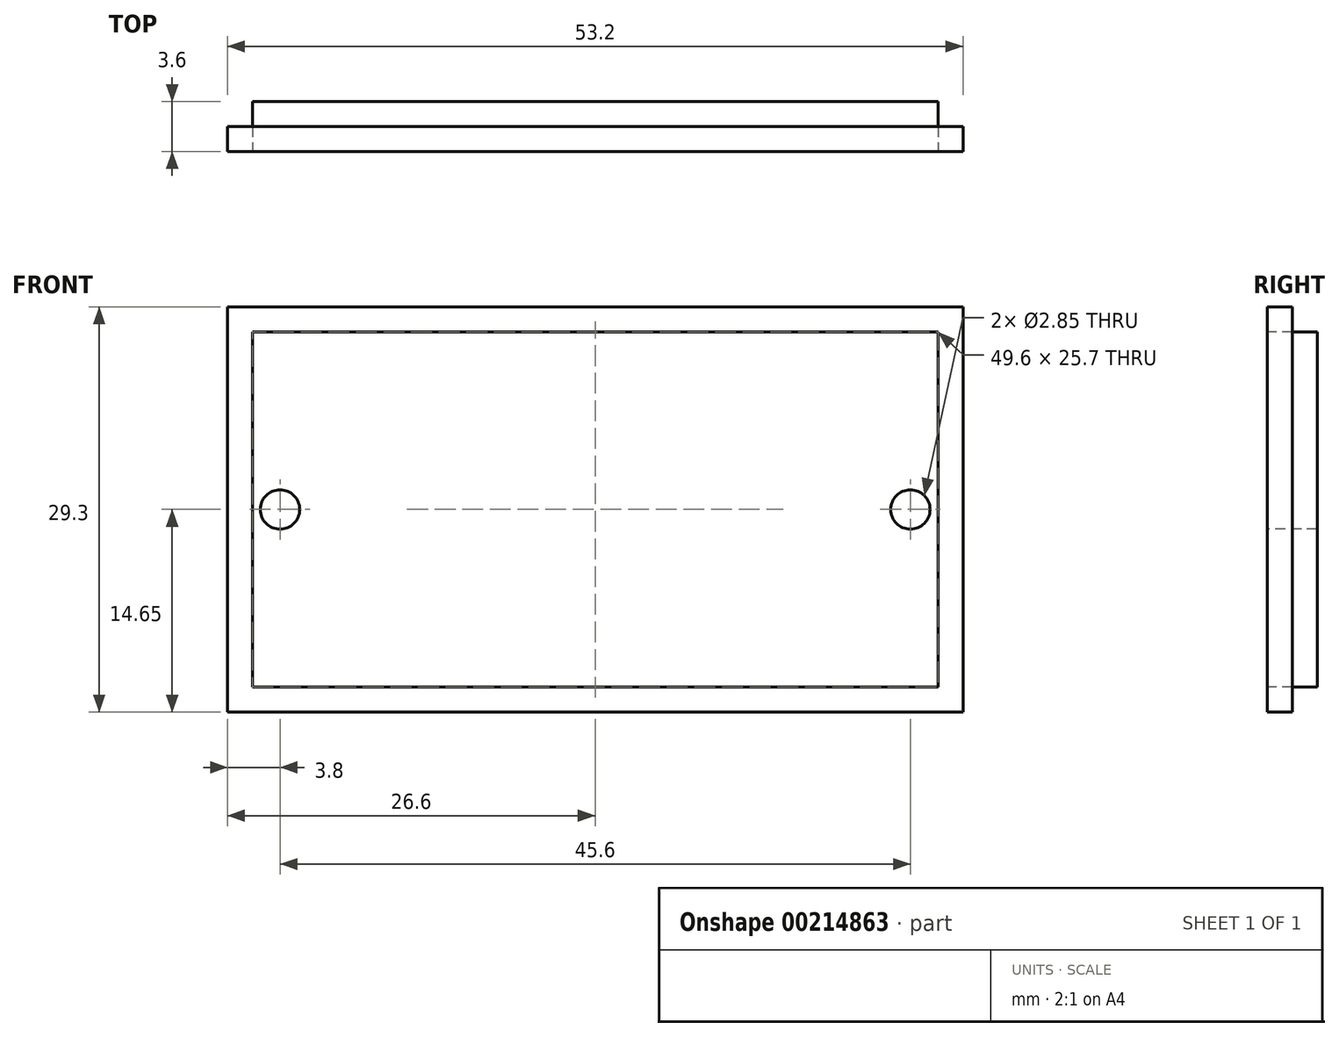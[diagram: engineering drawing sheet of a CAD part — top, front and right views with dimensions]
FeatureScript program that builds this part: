
annotation { "Feature Type Name" : "Feature", "Feature Type Description" : "" }
export const myFeature = defineFeature(function(context is Context, id is Id, definition is map)
    precondition{}
    {
        {
            var Q0;
            Q0=qCreatedBy(makeId("Front.planeOp"),FACE);
            var sketch = newSketch(context, id + "F0", { "sketchPlane" : qUnion([Q0])});
            skLineSegment(sketch, "E0.bottom", {"start": v(24.8, -12.85) * mm, "end": v(-24.8, -12.85) * mm});
            skLineSegment(sketch, "E0.top", {"start": v(24.8, 12.85) * mm, "end": v(-24.8, 12.85) * mm});
            skLineSegment(sketch, "E0.left", {"start": v(24.8, -12.85) * mm, "end": v(24.8, 12.85) * mm});
            skLineSegment(sketch, "E0.right", {"start": v(-24.8, -12.85) * mm, "end": v(-24.8, 12.85) * mm});
            skPoint(sketch, "E0.middle", {"position": v(0, 0) * mm});
            skLineSegment(sketch, "E1.0", {"start": v(26.6, 14.65) * mm, "end": v(-26.6, 14.65) * mm});
            skLineSegment(sketch, "E1.1", {"start": v(26.6, -14.65) * mm, "end": v(26.6, 14.65) * mm});
            skLineSegment(sketch, "E1.2", {"start": v(26.6, -14.65) * mm, "end": v(-26.6, -14.65) * mm});
            skLineSegment(sketch, "E1.3", {"start": v(-26.6, -14.65) * mm, "end": v(-26.6, 14.65) * mm});
            skCircle(sketch, "E2", {"center": v(-22.8, 0) * mm, "radius": 1.43 * mm});
            skCircle(sketch, "E3.MirrorC", {"center": v(22.8, 0) * mm, "radius": 1.43 * mm});
            skSolve(sketch);
        }
        {
            var Q0;
            Q0=makeQuery(id+"F0.imprint","IMPRINT",FACE,{"disambiguationData":[TD([[makeQuery(id+"F0.imprint","IMPRINT",EDGE,{"derivedFrom":sQuery(id+"F0.wireOp",EDGE,"E0.bottom")}),-1.0]])]});
            extrude(context, id + "F1", {"entities" : qUnion([Q0]), "oppositeDirection" : true, "depth" : 3.6 * mm});
        }
        {
            var Q0;
            Q0=makeQuery(id+"F0.imprint","IMPRINT",FACE,{"disambiguationData":[TD([[makeQuery(id+"F0.imprint","IMPRINT",EDGE,{"derivedFrom":sQuery(id+"F0.wireOp",EDGE,"E0.bottom")}),1.0]])]});
            var Q1;
            Q1=sQuery(id+"F0.wireOp",EDGE,"E1.0");
            var Q2;
            Q2=sQuery(id+"F0.wireOp",EDGE,"E1.1");
            var Q3;
            Q3=sQuery(id+"F0.wireOp",EDGE,"E0.top");
            var Q4;
            Q4=sQuery(id+"F0.wireOp",EDGE,"E0.left");
            var Q5;
            Q5=sQuery(id+"F0.wireOp",EDGE,"E0.bottom");
            var Q6;
            Q6=sQuery(id+"F0.wireOp",EDGE,"E1.2");
            var Q7;
            Q7=sQuery(id+"F0.wireOp",EDGE,"E1.3");
            var Q8;
            Q8=sQuery(id+"F0.wireOp",EDGE,"E0.right");
            extrude(context, id + "F2", {"entities" : qUnion([Q0]), "surfaceEntities" : qUnion([Q1, Q2, Q3, Q4, Q5, Q6, Q7, Q8]), "oppositeDirection" : true, "depth" : 1.8 * mm});
        }
    });
